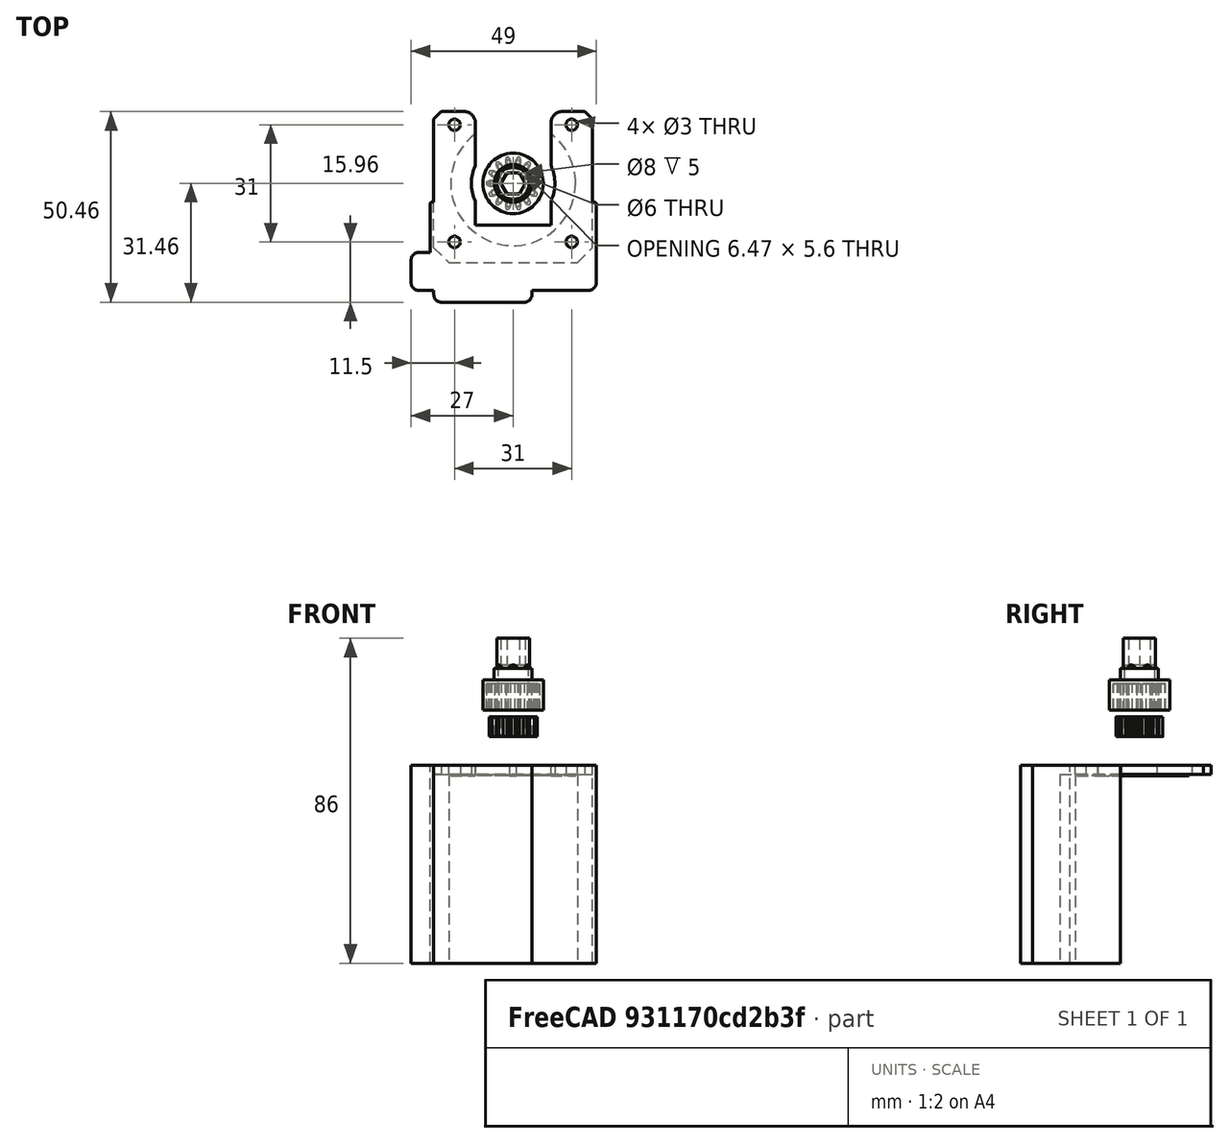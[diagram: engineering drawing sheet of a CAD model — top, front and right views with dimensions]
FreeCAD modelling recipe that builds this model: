
FCSTD DOCUMENT  (FreeCAD 0.19R24366 (Git))
Label: stepper_housing_assy
License: All rights reserved
LicenseURL: http://en.wikipedia.org/wiki/All_rights_reserved
objects: Sketcher::SketchObject×23, PartDesign::Pad×13, PartDesign::Pocket×10, PartDesign::Fillet×5, PartDesign::Body×3, PartDesign::Mirrored×3, Part::Part2DObjectPython×2, PartDesign::Hole×2, PartDesign::Plane×2, Mesh::Feature×2, PartDesign::PolarPattern×1
note: 94 computed .brp shape members not serialized (recipe doc carries the construction recipe); baked Part::Feature solids carry a one-line shape summary decoded from their .brp

FEATURE [Part::Part2DObjectPython] InvoluteGear  # Draft 2D object (typed FeaturePython)
  ExternalGear = true
  HighPrecision = true
  Modules = 0.79
  NumberOfTeeth = 14
  PressureAngle = 20
FEATURE [PartDesign::Pad] Pad
  Direction = (1,1,1)
  Length = 5.2
  Length2 = 100
  Profile = -> InvoluteGear
  Refine = true
  Type = 0
FEATURE [Sketcher::SketchObject] Sketch
  FullyConstrained = true
  MapMode = 5
  Placement = pos=(0,0,5.2) rot=(0,0,1;0rad)
  Support = -> [Pad]
  sketch-geometry (1):
    g0: Circle CenterX=0 CenterY=0 CenterZ=0 NormalX=0 NormalY=0 NormalZ=1 AngleXU=0 Radius=2.5
  constraints (2):
    c: Coincident(g0,g-1)
    c: Diameter(g0) = 5
FEATURE [PartDesign::Hole] Hole
  BaseFeature = -> Pad
  Depth = 25
  DepthType = 0
  Diameter = 6
  DrillForDepth = false
  DrillPoint = 1
  DrillPointAngle = 118
  HoleCutCountersinkAngle = 90
  HoleCutCustomValues = false
  HoleCutDepth = 0
  HoleCutDiameter = 6.1
  HoleCutType = 0
  ModelActualThread = false
  Profile = -> Sketch
  Refine = true
  Tapered = false
  TaperedAngle = 90
  ThreadAngle = 0
  ThreadClass = 0
  ThreadCutOffInner = 0
  ThreadCutOffOuter = 0
  ThreadDirection = 0
  ThreadFit = 0
  ThreadPitch = 0
  ThreadSize = 0
  ThreadType = 0
  Threaded = false
FEATURE [PartDesign::Body] Body  label="stepper_gear"
  Group = -> [InvoluteGear,Pad,Sketch,Hole]
  Origin = -> Origin
  Placement = pos=(0,0,20) rot=(0,0,1;0rad)
  Tip = -> Hole
FEATURE [Sketcher::SketchObject] Sketch001
  FullyConstrained = true
  MapMode = 5
  Support = -> [XY_Plane001]
  sketch-geometry (1):
    g0: Circle CenterX=0 CenterY=0 CenterZ=0 NormalX=0 NormalY=0 NormalZ=1 AngleXU=0 Radius=8
  constraints (2):
    c: Coincident(g0,g-1)
    c: Diameter(g0) = 16
FEATURE [PartDesign::Pad] Pad001
  Direction = (1,1,1)
  Length = 8
  Length2 = 100
  Profile = -> Sketch001
  Refine = true
  Type = 0
FEATURE [Sketcher::SketchObject] Sketch002
  FullyConstrained = true
  MapMode = 5
  Placement = pos=(0,0,8) rot=(0,0,1;0rad)
  Support = -> [Pad001]
  sketch-geometry (1):
    g0: Circle CenterX=0 CenterY=0 CenterZ=0 NormalX=0 NormalY=0 NormalZ=1 AngleXU=0 Radius=5
  constraints (2):
    c: Coincident(g0,g-1)
    c: Diameter(g0) = 10
FEATURE [PartDesign::Pad] Pad002
  BaseFeature = -> Pad001
  Direction = (1,1,1)
  Length = 3
  Length2 = 100
  Profile = -> Sketch002
  Refine = true
  Type = 0
FEATURE [Sketcher::SketchObject] Sketch004
  FullyConstrained = true
  MapMode = 5
  Placement = pos=(0,0,11) rot=(0,0,1;0rad)
  Support = -> [Pad002]
  sketch-geometry (1):
    g0: Circle CenterX=0 CenterY=0 CenterZ=0 NormalX=0 NormalY=0 NormalZ=1 AngleXU=0 Radius=4
  constraints (2):
    c: Coincident(g0,g-1)
    c: Diameter(g0) = 8
FEATURE [PartDesign::Hole] Hole001
  BaseFeature = -> Pad002
  Depth = 5
  DepthType = 0
  Diameter = 8
  DrillForDepth = false
  DrillPoint = 0
  DrillPointAngle = 118
  HoleCutCountersinkAngle = 90
  HoleCutCustomValues = false
  HoleCutDepth = 0
  HoleCutDiameter = 8.1
  HoleCutType = 0
  ModelActualThread = false
  Profile = -> Sketch004
  Refine = true
  Tapered = false
  TaperedAngle = 90
  ThreadAngle = 0
  ThreadClass = 0
  ThreadCutOffInner = 0
  ThreadCutOffOuter = 0
  ThreadDirection = 0
  ThreadFit = 0
  ThreadPitch = 0
  ThreadSize = 0
  ThreadType = 0
  Threaded = false
FEATURE [PartDesign::Plane] DatumPlane
  Length = 60
  MapMode = 5
  Placement = pos=(0,0,11) rot=(0,0,1;0rad)
  ResizeMode = 0
  Support = -> [Hole001]
  Width = 60
FEATURE [Sketcher::SketchObject] Sketch013
  FullyConstrained = true
  MapMode = 5
  Placement = pos=(0,0,11) rot=(0,0,1;0rad)
  Support = -> [DatumPlane]
  sketch-geometry (1):
    g0: Circle CenterX=0 CenterY=0 CenterZ=0 NormalX=0 NormalY=0 NormalZ=1 AngleXU=0 Radius=4
  constraints (2):
    c: Coincident(g0,g-1)
    c: Diameter(g0) = 8
FEATURE [PartDesign::Pad] Pad008
  BaseFeature = -> Hole001
  Direction = (1,1,1)
  Length = 1
  Length2 = 100
  Profile = -> Sketch013
  Refine = true
  Reversed = true
  Type = 0
FEATURE [Sketcher::SketchObject] Sketch014
  FullyConstrained = true
  MapMode = 5
  Placement = pos=(0,0,11) rot=(0,0,1;0rad)
  Support = -> [DatumPlane]
  sketch-geometry (1):
    g0: Circle CenterX=0 CenterY=0 CenterZ=0 NormalX=0 NormalY=0 NormalZ=1 AngleXU=0 Radius=4.3
  constraints (2):
    c: Coincident(g0,g-1)
    c: Diameter(g0) = 8.6
FEATURE [PartDesign::Pad] Pad009
  BaseFeature = -> Pad008
  Direction = (1,1,1)
  Length = 8
  Length2 = 100
  Profile = -> Sketch014
  Refine = true
  Type = 0
FEATURE [Sketcher::SketchObject] Sketch015
  FullyConstrained = true
  MapMode = 5
  Placement = pos=(0,0,19) rot=(0,0,1;0rad)
  Support = -> [Pad009]
  sketch-geometry (7):
    g0: LineSegment StartX=-1.61658 StartY=-2.8 StartZ=0 EndX=1.61658 EndY=-2.8 EndZ=0
    g1: LineSegment StartX=1.61658 StartY=-2.8 StartZ=0 EndX=3.23316 EndY=4e-16 EndZ=0
    g2: LineSegment StartX=3.23316 StartY=4e-16 StartZ=0 EndX=1.61658 EndY=2.8 EndZ=0
    g3: LineSegment StartX=1.61658 StartY=2.8 StartZ=0 EndX=-1.61658 EndY=2.8 EndZ=0
    g4: LineSegment StartX=-1.61658 StartY=2.8 StartZ=0 EndX=-3.23316 EndY=0 EndZ=0
    g5: LineSegment StartX=-3.23316 StartY=0 StartZ=0 EndX=-1.61658 EndY=-2.8 EndZ=0
    g6: Circle CenterX=0 CenterY=0 CenterZ=0 NormalX=0 NormalY=0 NormalZ=1 AngleXU=0 Radius=3.23316
  constraints (16):
    c: Coincident(g0,g1)
    c: Coincident(g1,g2)
    c: Coincident(g2,g3)
    c: Coincident(g3,g4)
    c: Coincident(g4,g5)
    c: Coincident(g5,g0)
    c: Equal(g0, g1-g5) x5
    c: PointOnObject(g0,g6)
    c: PointOnObject(g1,g6)
    c: PointOnObject(g2,g6)
    c: PointOnObject(g3,g6)
    c: PointOnObject(g4,g6)
    c: PointOnObject(g5,g6)
    c: Coincident(g6,g-1)
    c: Horizontal(g4,g-1)
    c: DistanceY(g0,g3) = 5.6
FEATURE [PartDesign::Pocket] Pocket005
  BaseFeature = -> Pad009
  Length = 9
  Length2 = 100
  Profile = -> Sketch015
  Refine = true
  Type = 0
FEATURE [Part::Part2DObjectPython] InvoluteGear005  # Draft 2D object (typed FeaturePython)
  ExternalGear = true
  HighPrecision = true
  Modules = 0.88
  NumberOfTeeth = 14
  PressureAngle = 20
FEATURE [PartDesign::Pocket] Pocket007
  BaseFeature = -> Pocket005
  Length = 7
  Length2 = 100
  Profile = -> InvoluteGear005
  Refine = true
  Reversed = true
  Type = 0
FEATURE [PartDesign::Plane] DatumPlane003
  AttachmentOffset = pos=(0,0,0) rot=(1,0,0;1.5708rad)
  Length = 60
  MapMode = 5
  Placement = pos=(0,0,19) rot=(1,0,0;1.5708rad)
  ResizeMode = 0
  Support = -> [Pocket007]
  Width = 60
FEATURE [Sketcher::SketchObject] Sketch034
  FullyConstrained = true
  MapMode = 5
  Placement = pos=(0,0,19) rot=(1,0,0;1.5708rad)
  Support = -> [DatumPlane003]
  sketch-geometry (2):
    g0: LineSegment StartX=1.25 StartY=-8 StartZ=0 EndX=-1.25 EndY=-8 EndZ=0
    g1: ArcOfCircle CenterX=0 CenterY=-8.35707 CenterZ=0 NormalX=0 NormalY=0 NormalZ=1 AngleXU=0 Radius=1.3 StartAngle=0.278247 EndAngle=2.86335
  constraints (6):
    c: Symmetric(g0,g0,g-2)
    c: DistanceY(g0) = -8
    c: Coincident(g1,g0)
    c: DistanceX(g0,g0) = 2.5
    c: Coincident(g1,g0)
    c: Radius(g1) = 1.3
FEATURE [PartDesign::Pocket] Pocket
  BaseFeature = -> Pocket007
  Length = 6
  Length2 = 100
  Profile = -> Sketch034
  Refine = true
  Reversed = true
  Type = 0
FEATURE [PartDesign::PolarPattern] PolarPattern001
  Angle = 360
  Axis = -> Z_Axis001
  BaseFeature = -> Pocket
  Occurrences = 6
  Originals = -> [Pocket]
  Refine = true
FEATURE [Sketcher::SketchObject] Sketch041
  FullyConstrained = true
  MapMode = 5
  Support = -> [XY_Plane006]
  sketch-geometry (8):
    g0: LineSegment StartX=-21 StartY=22 StartZ=0 EndX=-10 EndY=22 EndZ=0
    g1: LineSegment StartX=21 StartY=22 StartZ=0 EndX=21 EndY=-22 EndZ=0
    g2: LineSegment StartX=21 StartY=-22 StartZ=0 EndX=-21 EndY=-22 EndZ=0
    g3: LineSegment StartX=-21 StartY=-22 StartZ=0 EndX=-21 EndY=22 EndZ=0
    g4: LineSegment StartX=10 StartY=22 StartZ=0 EndX=10 EndY=-8 EndZ=0
    g5: LineSegment StartX=10 StartY=-8 StartZ=0 EndX=-10 EndY=-8 EndZ=0
    g6: LineSegment StartX=-10 StartY=-8 StartZ=0 EndX=-10 EndY=22 EndZ=0
    g7: LineSegment StartX=10 StartY=22 StartZ=0 EndX=21 EndY=22 EndZ=0
  constraints (21):
    c: Coincident(g7,g1)
    c: Coincident(g1,g2)
    c: Coincident(g2,g3)
    c: Coincident(g3,g0)
    c: Horizontal(g0)
    c: Horizontal(g2)
    c: Vertical(g1)
    c: Vertical(g3)
    c: Symmetric(g2,g7,g-1)
    c: DistanceY(g3,g3) = 44
    c: DistanceX(g0,g7) = 42
    c: Coincident(g4,g5)
    c: Coincident(g5,g6)
    c: Vertical(g4)
    c: Vertical(g6)
    c: Symmetric(g4,g5,g-2)
    c: DistanceY(g6,g6) = 30
    c: DistanceX(g5,g5) = 20
    c: Tangent(g0,g7)
    c: Coincident(g0,g6)
    c: Coincident(g7,g4)
FEATURE [PartDesign::Pad] Pad021
  Direction = (1,1,1)
  Length = 2.45
  Length2 = 100
  Profile = -> Sketch041
  Refine = true
  Type = 0
FEATURE [Sketcher::SketchObject] Sketch043
  ExternalGeometry = -> [Pad021]
  FullyConstrained = true
  MapMode = 5
  Placement = pos=(0,0,0) rot=(1,0,0;3.14159rad)
  Support = -> [Pad021]
  sketch-geometry (6):
    g0: LineSegment StartX=21 StartY=14 StartZ=0 EndX=21 EndY=22 EndZ=0
    g1: LineSegment StartX=21 StartY=22 StartZ=0 EndX=-21 EndY=22 EndZ=0
    g2: LineSegment StartX=-21 StartY=22 StartZ=0 EndX=-21 EndY=14 EndZ=0
    g3: LineSegment StartX=-21 StartY=14 StartZ=0 EndX=-17 EndY=18 EndZ=0
    g4: LineSegment StartX=-17 StartY=18 StartZ=0 EndX=17 EndY=18 EndZ=0
    g5: LineSegment StartX=17 StartY=18 StartZ=0 EndX=21 EndY=14 EndZ=0
  constraints (16):
    c: PointOnObject(g0,g-3)
    c: Coincident(g0,g-4)
    c: Coincident(g0,g1)
    c: Coincident(g1,g-5)
    c: Coincident(g1,g2)
    c: PointOnObject(g2,g-5)
    c: Coincident(g2,g3)
    c: Coincident(g3,g4)
    c: Coincident(g4,g5)
    c: Coincident(g5,g0)
    c: DistanceY(g0,g0) = 8
    c: DistanceY(g4,g0) = 4
    c: DistanceY(g2,g2) = 8
    c: DistanceX(g4,g0) = 4
    c: DistanceX(g1,g3) = 4
    c: DistanceY(g2,g3) = 4
FEATURE [PartDesign::Pad] Pad022
  BaseFeature = -> Pad021
  Direction = (1,1,1)
  Length = 50
  Length2 = 100
  Profile = -> Sketch043
  Refine = true
  Type = 0
FEATURE [Sketcher::SketchObject] Sketch044
  FullyConstrained = true
  MapMode = 5
  Placement = pos=(0,0,2.45) rot=(0,0,1;0rad)
  Support = -> [Pad022]
  sketch-geometry (2):
    g0: Circle CenterX=-15.5 CenterY=18.5 CenterZ=0 NormalX=0 NormalY=0 NormalZ=1 AngleXU=0 Radius=1.5
    g1: Circle CenterX=-15.5 CenterY=-12.5 CenterZ=0 NormalX=0 NormalY=0 NormalZ=1 AngleXU=0 Radius=1.5
  constraints (6):
    c: Radius(g0) = 1.5
    c: DistanceY(g-1,g0) = 18.5
    c: DistanceX(g0,g-1) = 15.5
    c: Radius(g1) = 1.5
    c: DistanceX(g1) = -15.5
    c: DistanceY(g1,g0) = 31
FEATURE [PartDesign::Pocket] Pocket019
  BaseFeature = -> Pad022
  Length = 5
  Length2 = 100
  Profile = -> Sketch044
  Refine = true
  Type = 0
FEATURE [PartDesign::Mirrored] Mirrored
  BaseFeature = -> Pocket019
  MirrorPlane = -> Sketch044 [V_Axis]
  Originals = -> [Pocket019]
  Refine = true
FEATURE [Sketcher::SketchObject] Sketch045
  ExternalGeometry = -> [Mirrored]
  FullyConstrained = true
  MapMode = 5
  Placement = pos=(-21,0,0) rot=(0.57735,-0.57735,-0.57735;2.0944rad)
  Support = -> [Mirrored]
  sketch-geometry (4):
    g0: LineSegment StartX=22 StartY=-50 StartZ=0 EndX=2 EndY=-50 EndZ=0
    g1: LineSegment StartX=2 StartY=-50 StartZ=0 EndX=2 EndY=2.45 EndZ=0
    g2: LineSegment StartX=2 StartY=2.45 StartZ=0 EndX=22 EndY=2.45 EndZ=0
    g3: LineSegment StartX=22 StartY=-50 StartZ=0 EndX=22 EndY=2.45 EndZ=0
  constraints (10):
    c: Coincident(g-4,g0)
    c: Coincident(g0,g1)
    c: Vertical(g1)
    c: Coincident(g1,g2)
    c: Coincident(g2,g-4)
    c: Coincident(g0,g3)
    c: Coincident(g3,g2)
    c: DistanceY(g-3,g0) = 0
    c: DistanceX(g0,g-3) = 12
    c: DistanceY(g1,g2) = 0
FEATURE [PartDesign::Pad] Pad023
  BaseFeature = -> Mirrored
  Direction = (1,1,1)
  Length = 1
  Length2 = 100
  Profile = -> Sketch045
  Refine = true
  Type = 0
FEATURE [PartDesign::Mirrored] Mirrored024
  BaseFeature = -> Pad023
  MirrorPlane = -> YZ_Plane006
  Originals = -> [Pad023]
  Refine = true
FEATURE [Sketcher::SketchObject] Sketch046
  ExternalGeometry = -> [Mirrored024]
  FullyConstrained = true
  MapMode = 5
  Placement = pos=(-1e-16,2e-16,2.45) rot=(0,0,1;0rad)
  Support = -> [Mirrored024]
  sketch-geometry (3):
    g0: LineSegment StartX=-21 StartY=20 StartZ=0 EndX=-13.2358 EndY=27.7642 EndZ=0
    g1: LineSegment StartX=-13.2358 StartY=27.7642 StartZ=0 EndX=-21 EndY=27.9575 EndZ=0
    g2: LineSegment StartX=-21 StartY=27.9575 StartZ=0 EndX=-21 EndY=20 EndZ=0
  constraints (9):
    c: Coincident(g0,g1)
    c: Coincident(g1,g2)
    c: Vertical(g2)
    c: Coincident(g0,g2)
    c: Angle(g0,g2) = 0.785398
    c: DistanceX(g0,g-4) = 0
    c: DistanceY(g0,g-4) = 2
    c: DistanceY(g1) = 27.9575
    c: DistanceX(g0) = -13.2358
FEATURE [PartDesign::Pocket] Pocket020
  BaseFeature = -> Mirrored024
  Length = 3
  Length2 = 100
  Profile = -> Sketch046
  Refine = true
  Type = 0
FEATURE [PartDesign::Mirrored] Mirrored025
  BaseFeature = -> Pocket020
  MirrorPlane = -> Sketch046 [V_Axis]
  Originals = -> [Pocket020]
  Refine = true
FEATURE [Sketcher::SketchObject] Sketch047
  ExternalGeometry = -> [Pad022]
  FullyConstrained = true
  MapMode = 5
  Placement = pos=(0,-22,0) rot=(1,0,0;1.5708rad)
  Support = -> [Pad022]
  sketch-geometry (4):
    g0: LineSegment StartX=-21 StartY=2.45 StartZ=0 EndX=5 EndY=2.45 EndZ=0
    g1: LineSegment StartX=5 StartY=2.45 StartZ=0 EndX=5 EndY=-50 EndZ=0
    g2: LineSegment StartX=5 StartY=-50 StartZ=0 EndX=-21 EndY=-50 EndZ=0
    g3: LineSegment StartX=-21 StartY=-50 StartZ=0 EndX=-21 EndY=2.45 EndZ=0
  constraints (12):
    c: Coincident(g0,g1)
    c: Coincident(g1,g2)
    c: Coincident(g2,g3)
    c: Coincident(g3,g0)
    c: Horizontal(g0)
    c: Horizontal(g2)
    c: Vertical(g1)
    c: Vertical(g3)
    c: DistanceX(g0,g0) = 26
    c: DistanceX(g-3,g0) = 0
    c: DistanceY(g0,g-3) = 0
    c: DistanceY(g-3,g2) = 0
FEATURE [PartDesign::Pad] Pad024
  BaseFeature = -> Mirrored025
  Direction = (1,1,1)
  Length = 6.46
  Length2 = 100
  Profile = -> Sketch047
  Refine = true
  Type = 0
FEATURE [Sketcher::SketchObject] Sketch048
  ExternalGeometry = -> [Pad024]
  FullyConstrained = true
  MapMode = 5
  Placement = pos=(-1.1e-15,-22,0) rot=(1,0,0;1.5708rad)
  Support = -> [Pad024]
  sketch-geometry (4):
    g0: LineSegment StartX=22 StartY=2.45 StartZ=0 EndX=5 EndY=2.45 EndZ=0
    g1: LineSegment StartX=5 StartY=2.45 StartZ=0 EndX=5 EndY=-50 EndZ=0
    g2: LineSegment StartX=5 StartY=-50 StartZ=0 EndX=22 EndY=-50 EndZ=0
    g3: LineSegment StartX=22 StartY=-50 StartZ=0 EndX=22 EndY=2.45 EndZ=0
  constraints (10):
    c: Coincident(g0,g1)
    c: Coincident(g1,g2)
    c: Coincident(g2,g3)
    c: Coincident(g3,g0)
    c: Horizontal(g0)
    c: Horizontal(g2)
    c: Vertical(g1)
    c: Vertical(g3)
    c: Coincident(g0,g-4)
    c: Coincident(g1,g-3)
FEATURE [PartDesign::Pad] Pad025
  BaseFeature = -> Pad024
  Direction = (1,1,1)
  Length = 3.31
  Length2 = 100
  Profile = -> Sketch048
  Refine = true
  Type = 0
FEATURE [Sketcher::SketchObject] Sketch049
  ExternalGeometry = -> [Pad025]
  FullyConstrained = true
  MapMode = 5
  Placement = pos=(-1.1e-15,-22,0) rot=(1,0,0;1.5708rad)
  Support = -> [Pad025]
  sketch-geometry (4):
    g0: LineSegment StartX=-21 StartY=2.45 StartZ=0 EndX=-22 EndY=2.45 EndZ=0
    g1: LineSegment StartX=-22 StartY=2.45 StartZ=0 EndX=-22 EndY=-50 EndZ=0
    g2: LineSegment StartX=-22 StartY=-50 StartZ=0 EndX=-21 EndY=-50 EndZ=0
    g3: LineSegment StartX=-21 StartY=-50 StartZ=0 EndX=-21 EndY=2.45 EndZ=0
  constraints (10):
    c: Coincident(g0,g1)
    c: Coincident(g1,g2)
    c: Coincident(g2,g3)
    c: Coincident(g3,g0)
    c: Horizontal(g0)
    c: Horizontal(g2)
    c: Vertical(g1)
    c: Vertical(g3)
    c: Coincident(g0,g-3)
    c: Coincident(g1,g-4)
FEATURE [PartDesign::Pad] Pad026
  BaseFeature = -> Pad025
  Direction = (1,1,1)
  Length = 3.31
  Length2 = 100
  Profile = -> Sketch049
  Refine = true
  Type = 0
FEATURE [PartDesign::Fillet] Fillet002
  Base = -> Pad026 [Edge68,Edge75]
  BaseFeature = -> Pad026
  Radius = 2
  Refine = true
  SupportTransform = false
FEATURE [PartDesign::Fillet] Fillet003
  Base = -> Fillet002 [Edge3]
  BaseFeature = -> Fillet002
  Radius = 2
  Refine = true
  SupportTransform = false
FEATURE [Sketcher::SketchObject] Sketch050
  ExternalGeometry = -> [Fillet003]
  FullyConstrained = true
  MapMode = 5
  Placement = pos=(-22,0,0) rot=(0.57735,-0.57735,-0.57735;2.0944rad)
  Support = -> [Fillet003]
  sketch-geometry (4):
    g0: LineSegment StartX=25.31 StartY=-50 StartZ=0 EndX=15.31 EndY=-50 EndZ=0
    g1: LineSegment StartX=15.31 StartY=-50 StartZ=0 EndX=15.31 EndY=2.45 EndZ=0
    g2: LineSegment StartX=15.31 StartY=2.45 StartZ=0 EndX=25.31 EndY=2.45 EndZ=0
    g3: LineSegment StartX=25.31 StartY=2.45 StartZ=0 EndX=25.31 EndY=-50 EndZ=0
  constraints (11):
    c: Coincident(g0,g1)
    c: Coincident(g1,g2)
    c: Coincident(g2,g3)
    c: Coincident(g3,g0)
    c: Horizontal(g0)
    c: Horizontal(g2)
    c: Vertical(g1)
    c: Vertical(g3)
    c: Coincident(g0,g-3)
    c: PointOnObject(g1,g-4)
    c: DistanceX(g0,g0) = 10
FEATURE [PartDesign::Pad] Pad027
  BaseFeature = -> Fillet003
  Direction = (1,1,1)
  Length = 5
  Length2 = 100
  Profile = -> Sketch050
  Refine = true
  Type = 0
FEATURE [PartDesign::Fillet] Fillet004
  Base = -> Pad027 [Edge83,Edge80]
  BaseFeature = -> Pad027
  Radius = 2
  Refine = true
  SupportTransform = false
FEATURE [Sketcher::SketchObject] Sketch051
  ExternalGeometry = -> [Fillet004]
  FullyConstrained = true
  MapMode = 5
  Placement = pos=(0,0,0) rot=(1,0,0;3.14159rad)
  Support = -> [Fillet004]
  sketch-geometry (1):
    g0: Circle CenterX=0 CenterY=-3 CenterZ=0 NormalX=0 NormalY=0 NormalZ=1 AngleXU=0 Radius=11.04
  constraints (3):
    c: PointOnObject(g0,g-2)
    c: Radius(g0) = 11.04
    c: DistanceY(g0,g-3) = 15.5
FEATURE [PartDesign::Pocket] Pocket021
  BaseFeature = -> Fillet004
  Length = 5
  Length2 = 100
  Profile = -> Sketch051
  Refine = true
  Type = 0
FEATURE [Sketcher::SketchObject] Sketch052
  ExternalGeometry = -> [Pad027]
  FullyConstrained = true
  MapMode = 5
  Placement = pos=(0,0,0) rot=(1,0,0;3.14159rad)
  Support = -> [Pad027]
  sketch-geometry (1):
    g0: Circle CenterX=0 CenterY=-3 CenterZ=0 NormalX=0 NormalY=0 NormalZ=1 AngleXU=0 Radius=11.04
  constraints (3):
    c: PointOnObject(g0,g-2)
    c: Radius(g0) = 11.04
    c: DistanceY(g0,g-3) = 15.5
FEATURE [PartDesign::Pocket] Pocket022
  BaseFeature = -> Pocket021
  Length = 5
  Length2 = 100
  Profile = -> Sketch052
  Refine = true
  Type = 0
FEATURE [Sketcher::SketchObject] Sketch053
  ExternalGeometry = -> [Pocket022]
  FullyConstrained = true
  MapMode = 5
  Placement = pos=(0,0,0) rot=(1,0,0;3.14159rad)
  Support = -> [Pocket022]
  sketch-geometry (1):
    g0: Circle CenterX=0 CenterY=-3 CenterZ=0 NormalX=0 NormalY=0 NormalZ=1 AngleXU=0 Radius=16.5
  constraints (3):
    c: PointOnObject(g0,g-2)
    c: Radius(g0) = 16.5
    c: DistanceY(g0,g-3) = 15.5
FEATURE [PartDesign::Pad] Pad028
  BaseFeature = -> Pocket022
  Direction = (1,1,1)
  Length = 0.35
  Length2 = 100
  Profile = -> Sketch053
  Refine = true
  Type = 0
FEATURE [Sketcher::SketchObject] Sketch054
  ExternalGeometry = -> [Pad028]
  FullyConstrained = true
  MapMode = 5
  Support = -> [Pad028]
  sketch-geometry (4):
    g0: LineSegment StartX=-10 StartY=-8 StartZ=0 EndX=10 EndY=-8 EndZ=0
    g1: LineSegment StartX=10 StartY=-8 StartZ=0 EndX=10 EndY=23.6 EndZ=0
    g2: LineSegment StartX=10 StartY=23.6 StartZ=0 EndX=-10 EndY=23.6 EndZ=0
    g3: LineSegment StartX=-10 StartY=23.6 StartZ=0 EndX=-10 EndY=-8 EndZ=0
  constraints (11):
    c: Coincident(g0,g1)
    c: Coincident(g1,g2)
    c: Coincident(g2,g3)
    c: Coincident(g3,g0)
    c: Horizontal(g2)
    c: Vertical(g1)
    c: Vertical(g3)
    c: DistanceX(g0,g0) = 20
    c: Symmetric(g0,g0,g-2)
    c: DistanceY(g-8,g0) = 0
    c: DistanceY(g1,g1) = 31.6
FEATURE [PartDesign::Pocket] Pocket023
  BaseFeature = -> Pad028
  Length = 5
  Length2 = 100
  Profile = -> Sketch054
  Refine = true
  Type = 0
FEATURE [Sketcher::SketchObject] Sketch055
  ExternalGeometry = -> [Pocket023]
  FullyConstrained = true
  MapMode = 5
  Placement = pos=(-2e-16,3e-16,2.45) rot=(0,0,1;0rad)
  Support = -> [Pocket023]
  sketch-geometry (1):
    g0: Circle CenterX=0 CenterY=3 CenterZ=0 NormalX=0 NormalY=0 NormalZ=1 AngleXU=0 Radius=11.04
  constraints (3):
    c: PointOnObject(g0,g-2)
    c: Radius(g0) = 11.04
    c: DistanceY(g-4,g0) = 15.5
FEATURE [PartDesign::Pocket] Pocket024
  BaseFeature = -> Pocket023
  Length = 5
  Length2 = 100
  Profile = -> Sketch055
  Refine = true
  Type = 0
FEATURE [PartDesign::Fillet] Fillet005
  Base = -> Pocket024 [Edge91,Edge109]
  BaseFeature = -> Pocket024
  Radius = 3
  Refine = true
  SupportTransform = false
FEATURE [PartDesign::Fillet] Fillet006
  Base = -> Fillet005 [Edge108,Edge56]
  BaseFeature = -> Fillet005
  Radius = 0.5
  Refine = true
  SupportTransform = false
FEATURE [PartDesign::Body] Body006  label="motor_mount"
  Group = -> [Sketch041,Pad021,Sketch043,Pad022,Sketch044,Pocket019,Mirrored,Sketch045,Pad023,Mirrored024,Sketch046,Pocket020,Mirrored025,Sketch047,Pad024,Sketch048,Pad025,Sketch049,Pad026,Fillet002,Fillet003,Sketch050,Pad027,Fillet004,Sketch051,Pocket021,Sketch052,Pocket022,Sketch053,Pad028,Sketch054,Pocket023,Sketch055,Pocket024,Fillet005,Fillet006]
  Origin = -> Origin006
  Placement = pos=(0,-3,10) rot=(0,0,1;0rad)
  Tip = -> Fillet006
FEATURE [Mesh::Feature] Mesh001  label="motor_mount_mesh"
FEATURE [Sketcher::SketchObject] Sketch056
  FullyConstrained = true
  MapMode = 5
  Placement = pos=(0,0,10) rot=(1,0,0;3.14159rad)
  Support = -> [PolarPattern001]
  sketch-geometry (1):
    g0: Circle CenterX=0 CenterY=0 CenterZ=0 NormalX=0 NormalY=0 NormalZ=1 AngleXU=0 Radius=4
  constraints (2):
    c: Coincident(g0,g-1)
    c: Radius(g0) = 4
FEATURE [PartDesign::Pocket] Pocket025
  BaseFeature = -> PolarPattern001
  Length = 2
  Length2 = 100
  Profile = -> Sketch056
  Refine = true
  Type = 0
FEATURE [PartDesign::Body] Body001  label="drive_shaft"
  Group = -> [Sketch001,Pad001,Sketch002,Pad002,Sketch004,Hole001,DatumPlane,Sketch013,Pad008,Sketch014,Pad009,Sketch015,Pocket005,InvoluteGear005,Pocket007,DatumPlane003,Sketch034,Pocket,PolarPattern001,Sketch056,Pocket025]
  Origin = -> Origin001
  Placement = pos=(0,0,27) rot=(0,0,1;0rad)
  Tip = -> Pocket025
FEATURE [Mesh::Feature] Mesh  label="drive_shaft (Meshed)"
